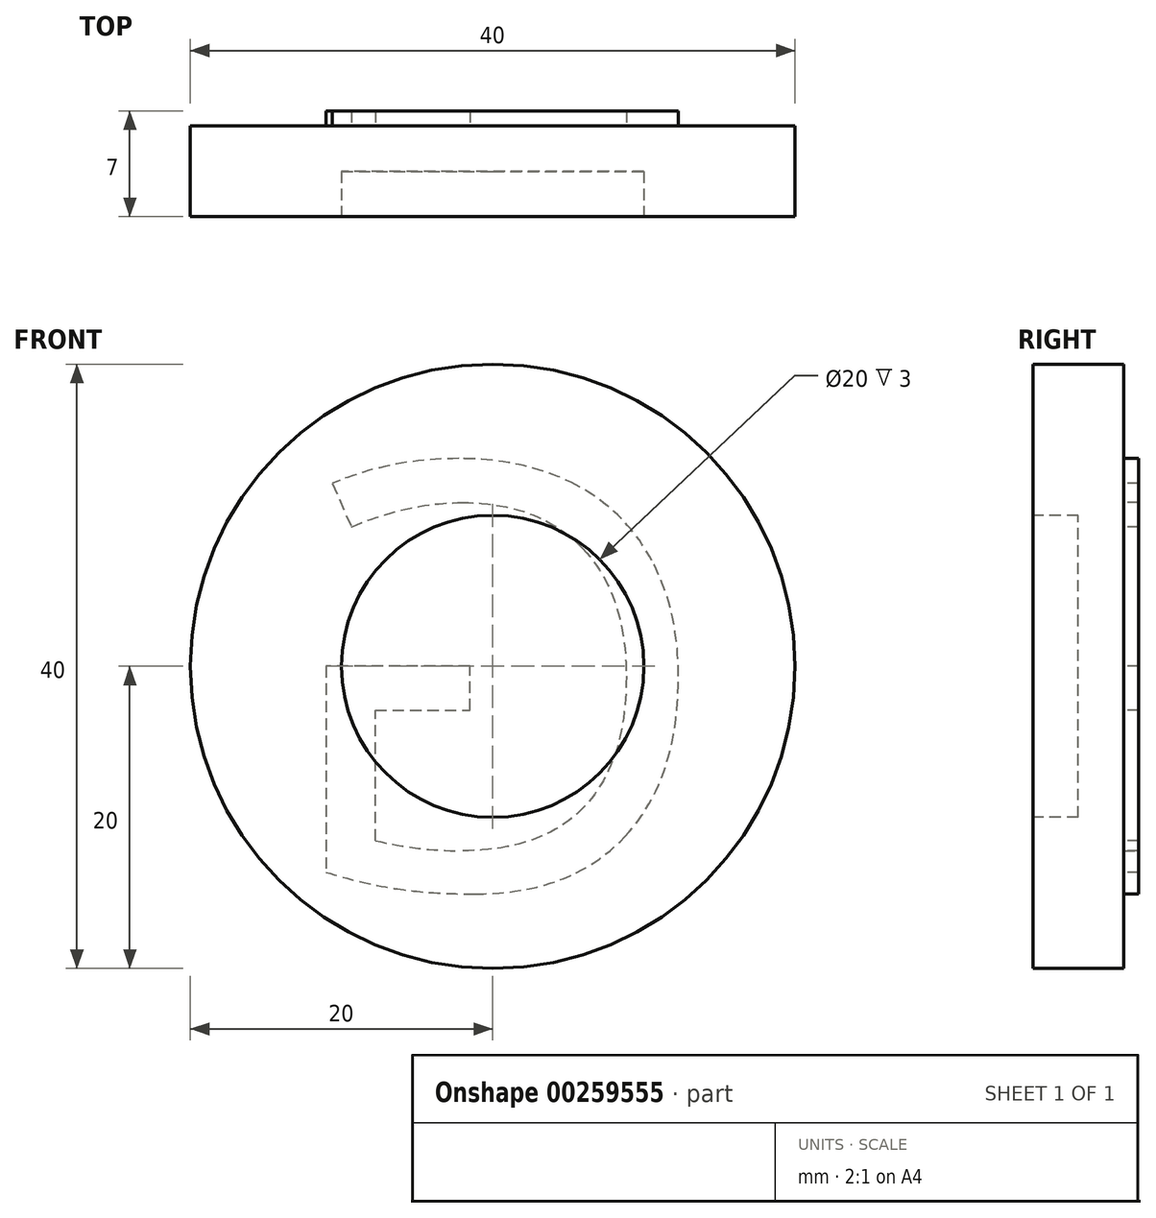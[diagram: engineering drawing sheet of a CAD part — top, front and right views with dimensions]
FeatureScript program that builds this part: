
annotation { "Feature Type Name" : "Feature", "Feature Type Description" : "" }
export const myFeature = defineFeature(function(context is Context, id is Id, definition is map)
    precondition{}
    {
        {
            var Q0;
            Q0=qCreatedBy(makeId("Front.planeOp"),FACE);
            var sketch = newSketch(context, id + "F0", { "sketchPlane" : qUnion([Q0])});
            skCircle(sketch, "E0", {"center": v(0, 0) * mm, "radius": 20 * mm});
            skCircle(sketch, "E1", {"center": v(0, 0) * mm, "radius": 10 * mm});
            skSolve(sketch);
        }
        {
            var Q0;
            Q0=makeQuery(id+"F0.imprint","IMPRINT",FACE,{"disambiguationData":[TD([[makeQuery(id+"F0.imprint","IMPRINT",EDGE,{"derivedFrom":sQuery(id+"F0.wireOp",EDGE,"E1")}),1.0]])]});
            var Q1;
            Q1=makeQuery(id+"F0.imprint","IMPRINT",FACE,{"disambiguationData":[TD([[makeQuery(id+"F0.imprint","IMPRINT",EDGE,{"derivedFrom":sQuery(id+"F0.wireOp",EDGE,"E0")}),1.0]])]});
            extrude(context, id + "F1", {"entities" : qUnion([Q0, Q1]), "depth" : 6 * mm});
        }
        {
            var Q0;
            Q0=makeQuery(id+"F1.opExtrude","CAP_FACE",FACE,{"disambiguationData":[OSD([sQuery(id+"F0.wireOp",EDGE,"E0")])],"isStart":false});
            var sketch = newSketch(context, id + "F2", { "sketchPlane" : qUnion([Q0])});
            skCircle(sketch, "E2", {"center": v(0, 0) * mm, "radius": 10 * mm});
            skSolve(sketch);
        }
        {
            var Q0;
            Q0=makeQuery(id+"F2.imprint","IMPRINT",FACE,{"disambiguationData":[TD([[makeQuery(id+"F2.imprint","IMPRINT",EDGE,{"derivedFrom":sQuery(id+"F2.wireOp",EDGE,"E2")}),1.0]])]});
            extrude(context, id + "F3", {"entities" : qUnion([Q0]), "operationType" : NewBodyOperationType.REMOVE, "oppositeDirection" : true, "depth" : 3 * mm});
        }
        {
            var Q0;
            Q0=makeQuery(id+"F1.opExtrude","CAP_FACE",FACE,{"disambiguationData":[OSD([sQuery(id+"F0.wireOp",EDGE,"E0")])],"isStart":true});
            var sketch = newSketch(context, id + "F4", { "sketchPlane" : qUnion([Q0])});
            skText(sketch, "E3", { "text": "G", "fontName": "OpenSans-Regular.ttf"});
            const initialGuessF4  = {"E3": [-0.01468, -0.01468, 1, 0, 0.02827]};
            skSetInitialGuess(sketch, initialGuessF4);
            skSolve(sketch);
        }
        {
            var Q0;
            Q0 = qSketchRegion(id + "F4", true);
            extrude(context, id + "F5", {"entities" : qUnion([Q0]), "operationType" : NewBodyOperationType.ADD, "depth" : 1 * mm});
        }
    });
